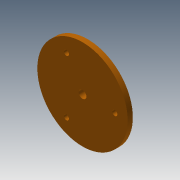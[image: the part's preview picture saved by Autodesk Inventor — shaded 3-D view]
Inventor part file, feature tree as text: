
AUTODESK INVENTOR PART (.ipt)
format: ipt  version: 2013 (Build 170138000, 138)  size: 108,544 bytes
history: native  units: mm
features: extrude x4, sketch x4
ambient origin geometry x8: Origin, YZ Plane, XZ Plane, XY Plane, X Axis, Y Axis, Z Axis, Center Point
bodies: Solid1 (feature_tree)
feature tree (8):
  extrude  "Extrusion1"  Depth=3.0mm
  extrude  "Extrusion2"  Depth=10.0mm
  extrude  "Extrusion3"  Depth=6.0mm
  extrude  "Extrusion4"  Depth=2.0mm
  sketch  "Sketch1"  dims[d0=35.0mm d1=3.0mm]
  sketch  "Sketch2"  dims[d2=2.0mm d3=0.0mm d4=10.0mm]
  sketch  "Sketch3"  dims[d5=3.8mm d6=0.0mm d7=6.0mm]
  sketch  "Sketch4"  dims[d8=3.8mm d9=0.0mm d11=2.0mm d12=120.0deg d13=120.0deg d14=2.0mm d15=2.0mm d16=3.8mm d17=0.0mm]
